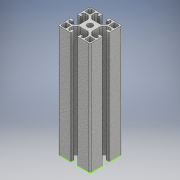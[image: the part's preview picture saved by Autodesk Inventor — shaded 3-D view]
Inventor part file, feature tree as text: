
AUTODESK INVENTOR PART (.ipt)
format: ipt  version: 2018.3 (Build 223284000, 284)  size: 334,848 bytes
history: native  units: mm
features: extrude x1, sketch x1
ambient origin geometry x8: Origin, YZ Plane, XZ Plane, XY Plane, X Axis, Y Axis, Z Axis, Center Point
bodies: Body1 (feature_tree)
feature tree (2):
  extrude  "Extrusión1"  [1 undecoded]
  sketch  "Boceto1"  dims[d0=140.0mm d1=0.0mm]
note: 1 required parameter value undecoded (feature->parameter linkage not recoverable at this tier; creation-order binding heuristic only, values carry confidence <= 0.55)
